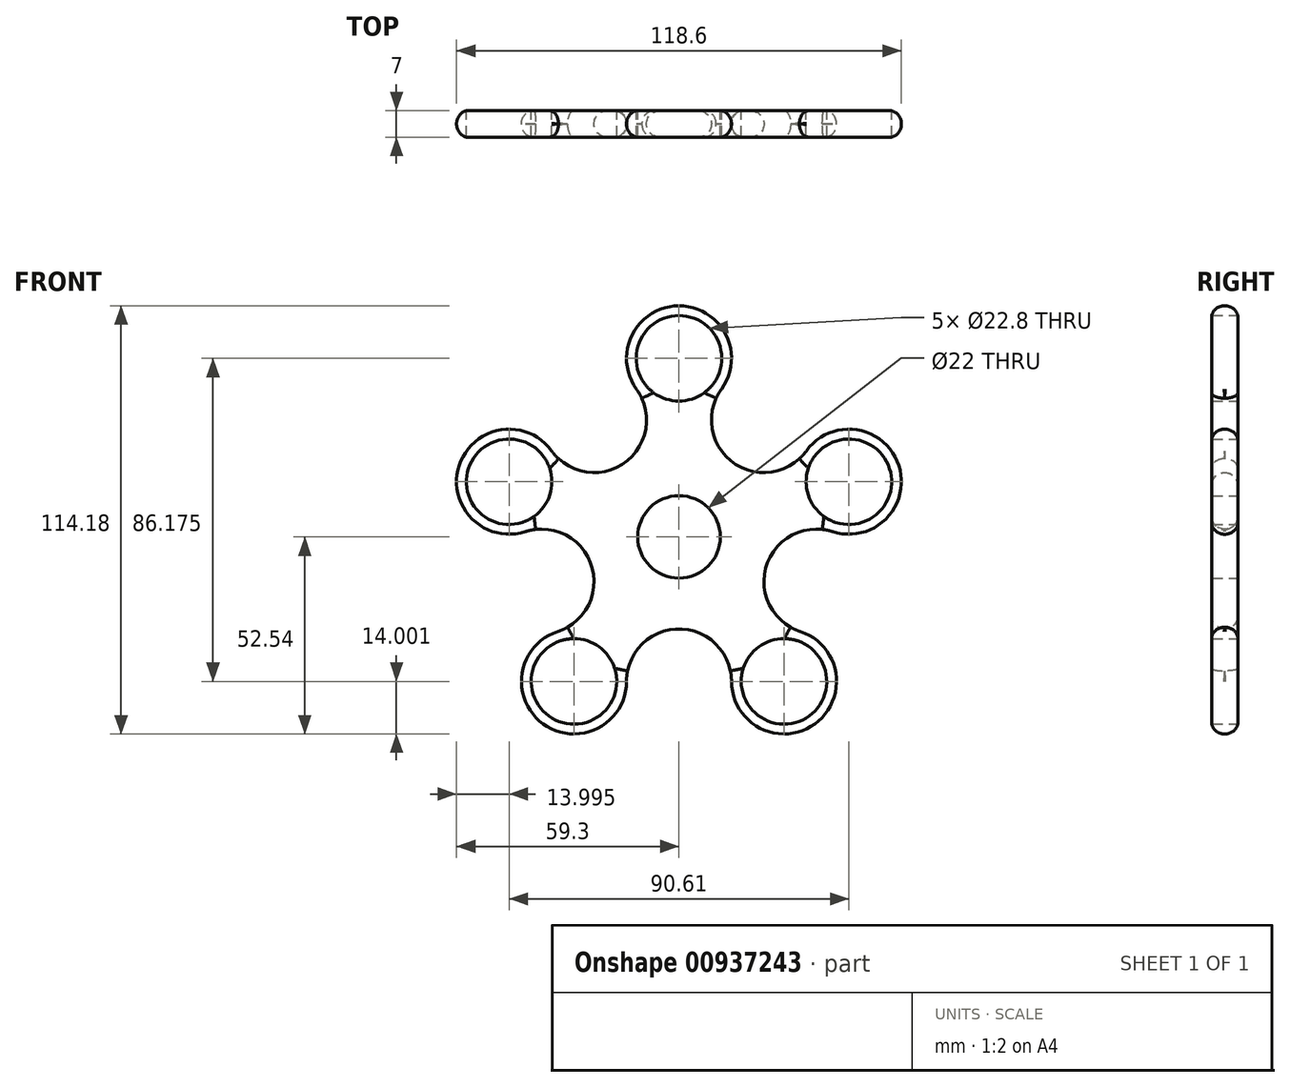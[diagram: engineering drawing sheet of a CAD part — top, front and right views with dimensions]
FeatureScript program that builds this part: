
annotation { "Feature Type Name" : "Feature", "Feature Type Description" : "" }
export const myFeature = defineFeature(function(context is Context, id is Id, definition is map)
    precondition{}
    {
        {
            var Q0;
            Q0=qCreatedBy(makeId("Front.planeOp"),FACE);
            var sketch = newSketch(context, id + "F0", { "sketchPlane" : qUnion([Q0])});
            skCircle(sketch, "E0", {"center": v(0, 0) * mm, "radius": 11 * mm});
            skArc(sketch, "E1.cCircle", {"start": v(-32.3, 21.03) * mm, "mid": v(-32.44, 20.8) * mm, "end": v(-32.59, 20.57) * mm, "construction": true});
            skPoint(sketch, "E1.0.midPoint", {"position": v(0, -38.54) * mm});
            skCircle(sketch, "E2", {"center": v(0, 47.64) * mm, "radius": 11.4 * mm});
            skCircle(sketch, "E3", {"center": v(0, 47.64) * mm, "radius": 14 * mm});
            skCircle(sketch, "E4", {"center": v(45.3, 14.72) * mm, "radius": 11.4 * mm});
            skCircle(sketch, "E5", {"center": v(45.3, 14.72) * mm, "radius": 14 * mm});
            skCircle(sketch, "E6", {"center": v(28, -38.54) * mm, "radius": 11.4 * mm});
            skCircle(sketch, "E7", {"center": v(28, -38.54) * mm, "radius": 14 * mm});
            skCircle(sketch, "E8", {"center": v(-28, -38.54) * mm, "radius": 11.4 * mm});
            skCircle(sketch, "E9", {"center": v(-28, -38.54) * mm, "radius": 14 * mm});
            skCircle(sketch, "E10", {"center": v(-45.3, 14.72) * mm, "radius": 11.4 * mm});
            skCircle(sketch, "E11", {"center": v(-45.3, 14.72) * mm, "radius": 14 * mm});
            skArc(sketch, "E12", {"start": v(11.33, 39.4) * mm, "mid": v(14.42, 19.85) * mm, "end": v(33.98, 22.95) * mm});
            skArc(sketch, "E13.1.0", {"start": v(-33.98, 22.95) * mm, "mid": v(-14.42, 19.85) * mm, "end": v(-11.33, 39.4) * mm});
            skArc(sketch, "E13.2.0", {"start": v(-32.33, -25.22) * mm, "mid": v(-23.34, -7.58) * mm, "end": v(-40.98, 1.4) * mm});
            skArc(sketch, "E13.3.0", {"start": v(14, -38.54) * mm, "mid": v(0, -24.54) * mm, "end": v(-14, -38.54) * mm});
            skArc(sketch, "E13.4.0", {"start": v(40.98, 1.4) * mm, "mid": v(23.34, -7.58) * mm, "end": v(32.33, -25.22) * mm});
            skArc(sketch, "E14.trimOffspring", {"start": v(10.02, 37.21) * mm, "mid": v(9.76, 37.28) * mm, "end": v(9.5, 37.35) * mm, "construction": true});
            skArc(sketch, "E15.trimOffspring", {"start": v(38.49, 1.97) * mm, "mid": v(38.47, 2.24) * mm, "end": v(38.46, 2.5) * mm, "construction": true});
            skArc(sketch, "E16.trimOffspring", {"start": v(29.64, -24.63) * mm, "mid": v(29.8, -24.43) * mm, "end": v(29.98, -24.22) * mm, "construction": true});
            skArc(sketch, "E17.trimOffspring", {"start": v(32.59, 20.57) * mm, "mid": v(32.44, 20.8) * mm, "end": v(32.3, 21.03) * mm, "construction": true});
            skArc(sketch, "E18.trimOffspring", {"start": v(-9.5, 37.35) * mm, "mid": v(-9.76, 37.28) * mm, "end": v(-10.02, 37.21) * mm, "construction": true});
            skArc(sketch, "E19.trimOffspring", {"start": v(-38.46, 2.5) * mm, "mid": v(-38.47, 2.24) * mm, "end": v(-38.49, 1.97) * mm, "construction": true});
            skArc(sketch, "E20.trimOffspring", {"start": v(-29.98, -24.22) * mm, "mid": v(-29.8, -24.43) * mm, "end": v(-29.64, -24.63) * mm, "construction": true});
            skArc(sketch, "E21.trimOffspring", {"start": v(-14.27, -35.8) * mm, "mid": v(-14.02, -35.9) * mm, "end": v(-13.77, -36) * mm, "construction": true});
            skArc(sketch, "E22.trimOffspring", {"start": v(13.77, -36) * mm, "mid": v(14.02, -35.9) * mm, "end": v(14.27, -35.8) * mm, "construction": true});
            skSolve(sketch);
        }
        {
            var Q0;
            Q0 = qSketchRegion(id + "F0", true);
            extrude(context, id + "F1", {"entities" : qUnion([Q0]), "depth" : 7 * mm, "offsetDistance" : 25 * mm});
        }
        {
            var Q0;
            Q0=makeQuery(id+"F1.opExtrude","CAP_EDGE",EDGE,{"disambiguationData":[OSD([sQuery(id+"F0.wireOp",EDGE,"E11")])],"isStart":false});
            var Q1;
            Q1=makeQuery(id+"F1.opExtrude","CAP_EDGE",EDGE,{"disambiguationData":[OSD([sQuery(id+"F0.wireOp",EDGE,"E11")])],"isStart":true});
            var Q2;
            Q2=makeQuery(id+"F1.opExtrude","CAP_EDGE",EDGE,{"disambiguationData":[OSD([sQuery(id+"F0.wireOp",EDGE,"E13.2.0")])],"isStart":false});
            var Q3;
            Q3=makeQuery(id+"F1.opExtrude","CAP_EDGE",EDGE,{"disambiguationData":[OSD([sQuery(id+"F0.wireOp",EDGE,"E13.2.0")])],"isStart":true});
            var Q4;
            Q4=makeQuery(id+"F1.opExtrude","CAP_EDGE",EDGE,{"disambiguationData":[OSD([sQuery(id+"F0.wireOp",EDGE,"E9")])],"isStart":false});
            var Q5;
            Q5=makeQuery(id+"F1.opExtrude","CAP_EDGE",EDGE,{"disambiguationData":[OSD([sQuery(id+"F0.wireOp",EDGE,"E9")])],"isStart":true});
            var Q6;
            Q6=makeQuery(id+"F1.opExtrude","CAP_EDGE",EDGE,{"disambiguationData":[OSD([sQuery(id+"F0.wireOp",EDGE,"E13.3.0")])],"isStart":true});
            var Q7;
            Q7=makeQuery(id+"F1.opExtrude","CAP_EDGE",EDGE,{"disambiguationData":[OSD([sQuery(id+"F0.wireOp",EDGE,"E13.3.0")])],"isStart":false});
            var Q8;
            Q8=makeQuery(id+"F1.opExtrude","CAP_EDGE",EDGE,{"disambiguationData":[OSD([sQuery(id+"F0.wireOp",EDGE,"E7")])],"isStart":true});
            var Q9;
            Q9=makeQuery(id+"F1.opExtrude","CAP_EDGE",EDGE,{"disambiguationData":[OSD([sQuery(id+"F0.wireOp",EDGE,"E7")])],"isStart":false});
            var Q10;
            Q10=makeQuery(id+"F1.opExtrude","CAP_EDGE",EDGE,{"disambiguationData":[OSD([sQuery(id+"F0.wireOp",EDGE,"E13.4.0")])],"isStart":false});
            var Q11;
            Q11=makeQuery(id+"F1.opExtrude","CAP_EDGE",EDGE,{"disambiguationData":[OSD([sQuery(id+"F0.wireOp",EDGE,"E13.4.0")])],"isStart":true});
            var Q12;
            Q12=makeQuery(id+"F1.opExtrude","CAP_EDGE",EDGE,{"disambiguationData":[OSD([sQuery(id+"F0.wireOp",EDGE,"E5")])],"isStart":false});
            var Q13;
            Q13=makeQuery(id+"F1.opExtrude","CAP_EDGE",EDGE,{"disambiguationData":[OSD([sQuery(id+"F0.wireOp",EDGE,"E5")])],"isStart":true});
            var Q14;
            Q14=makeQuery(id+"F1.opExtrude","CAP_EDGE",EDGE,{"disambiguationData":[OSD([sQuery(id+"F0.wireOp",EDGE,"E12")])],"isStart":true});
            var Q15;
            Q15=makeQuery(id+"F1.opExtrude","CAP_EDGE",EDGE,{"disambiguationData":[OSD([sQuery(id+"F0.wireOp",EDGE,"E12")])],"isStart":false});
            var Q16;
            Q16=makeQuery(id+"F1.opExtrude","CAP_EDGE",EDGE,{"disambiguationData":[OSD([sQuery(id+"F0.wireOp",EDGE,"E3")])],"isStart":true});
            var Q17;
            Q17=makeQuery(id+"F1.opExtrude","CAP_EDGE",EDGE,{"disambiguationData":[OSD([sQuery(id+"F0.wireOp",EDGE,"E3")])],"isStart":false});
            var Q18;
            Q18=makeQuery(id+"F1.opExtrude","CAP_EDGE",EDGE,{"disambiguationData":[OSD([sQuery(id+"F0.wireOp",EDGE,"E13.1.0")])],"isStart":true});
            var Q19;
            Q19=makeQuery(id+"F1.opExtrude","CAP_EDGE",EDGE,{"disambiguationData":[OSD([sQuery(id+"F0.wireOp",EDGE,"E13.1.0")])],"isStart":false});
            fillet(context, id + "F2", {"entities" : qUnion([Q0, Q1, Q2, Q3, Q4, Q5, Q6, Q7, Q8, Q9, Q10, Q11, Q12, Q13, Q14, Q15, Q16, Q17, Q18, Q19]), "radius" : 3.5 * mm, "tangentPropagation" : true, "allowEdgeOverflow" : false});
        }
    });
